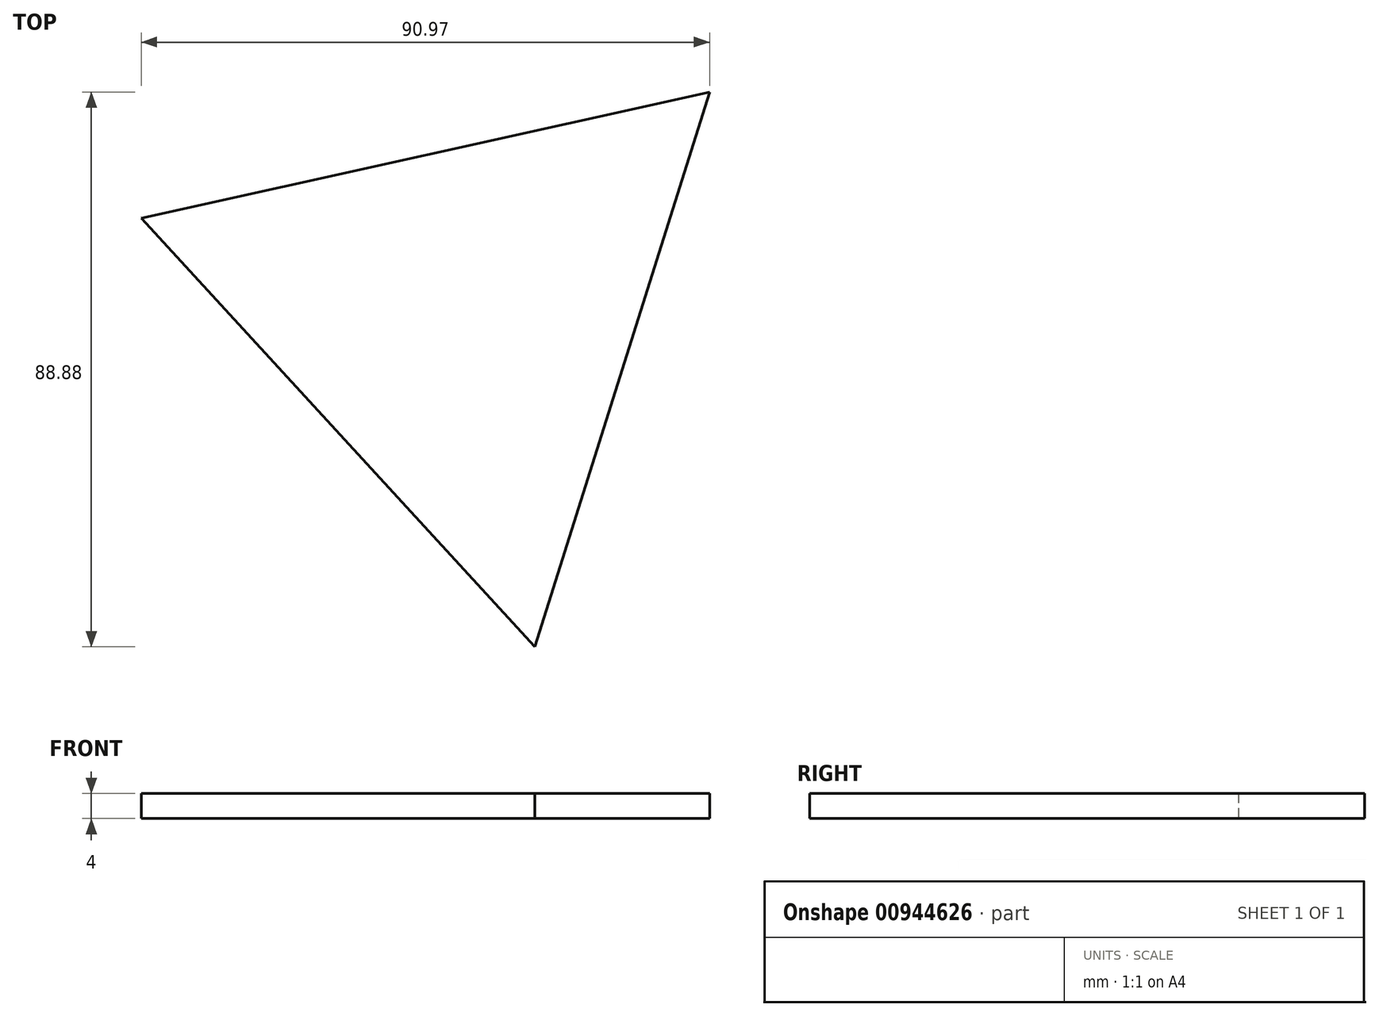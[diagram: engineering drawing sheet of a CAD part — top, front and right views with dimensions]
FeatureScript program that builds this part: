
annotation { "Feature Type Name" : "Feature", "Feature Type Description" : "" }
export const myFeature = defineFeature(function(context is Context, id is Id, definition is map)
    precondition{}
    {
        {
            var Q0;
            Q0=qCreatedBy(makeId("Top.planeOp"),FACE);
            var sketch = newSketch(context, id + "F0", { "sketchPlane" : qUnion([Q0])});
            skCircle(sketch, "E0.cCircle", {"center": v(-194.64, 76.85) * mm, "radius": 26.9 * mm, "construction": true});
            skLineSegment(sketch, "E0.0", {"start": v(-154.98, 113.2) * mm, "end": v(-182.98, 24.33) * mm});
            skLineSegment(sketch, "E0.1", {"start": v(-182.98, 24.33) * mm, "end": v(-245.95, 93.02) * mm});
            skLineSegment(sketch, "E0.2", {"start": v(-245.95, 93.02) * mm, "end": v(-154.98, 113.2) * mm});
            skPoint(sketch, "E0.0.midPoint", {"position": v(-168.98, 68.77) * mm});
            skSolve(sketch);
        }
        {
            var Q0;
            Q0=makeQuery(id+"F0.imprint","IMPRINT",FACE,{"disambiguationData":[TD([[makeQuery(id+"F0.imprint","IMPRINT",EDGE,{"derivedFrom":sQuery(id+"F0.wireOp",EDGE,"E0.0")}),-1.0]])]});
            extrude(context, id + "F1", {"entities" : qUnion([Q0]), "depth" : 4 * mm, "offsetDistance" : 25.4 * mm});
        }
    });
